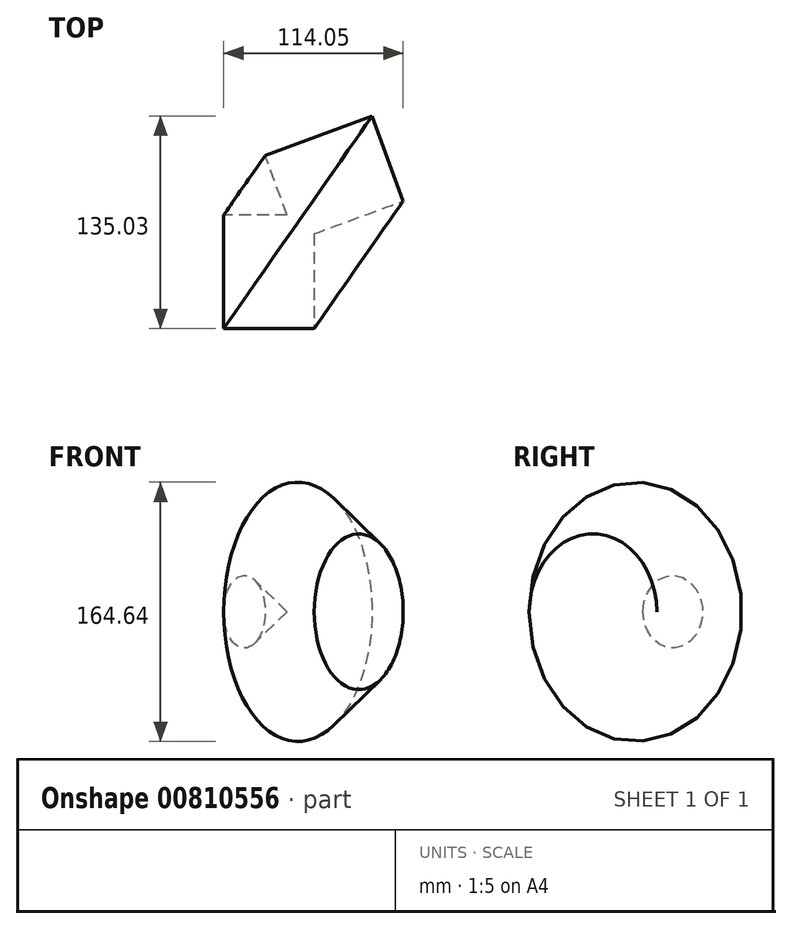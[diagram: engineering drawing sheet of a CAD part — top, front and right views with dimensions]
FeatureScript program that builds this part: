
annotation { "Feature Type Name" : "Feature", "Feature Type Description" : "" }
export const myFeature = defineFeature(function(context is Context, id is Id, definition is map)
    precondition{}
    {
        {
            var Q0;
            Q0=qCreatedBy(makeId("Top.planeOp"),FACE);
            var sketch = newSketch(context, id + "F0", { "sketchPlane" : qUnion([Q0])});
            skLineSegment(sketch, "E0.bottom", {"start": v(-26.2, 43.52) * mm, "end": v(31.26, 43.52) * mm});
            skLineSegment(sketch, "E0.top", {"start": v(-26.2, -28.75) * mm, "end": v(31.26, -28.75) * mm});
            skLineSegment(sketch, "E0.left", {"start": v(-26.2, 43.52) * mm, "end": v(-26.2, -28.75) * mm});
            skLineSegment(sketch, "E0.right", {"start": v(31.26, 43.52) * mm, "end": v(31.26, -28.75) * mm});
            skLineSegment(sketch, "E1", {"start": v(-12.84, 62.3) * mm, "end": v(48.34, 19.62) * mm});
            skSolve(sketch);
        }
        {
            var Q0;
            {var subQ1=sQuery(id+"F0.wireOp",EDGE,"E0.top");Q0=makeQuery(id+"F0.imprint","IMPRINT",FACE,{"disambiguationData":[TD([[makeQuery(id+"F0.imprint","IMPRINT",EDGE,{"derivedFrom":subQ1}),1.0]])]});}
            var Q1;
            Q1=sQuery(id+"F0.wireOp",EDGE,"E1");
            revolve(context, id + "F1", {"surfaceOperationType" : NewSurfaceOperationType.NEW, "entities" : qUnion([Q0]), "axis" : qUnion([Q1]), "revolveType" : RevolveType.FULL});
        }
    });
